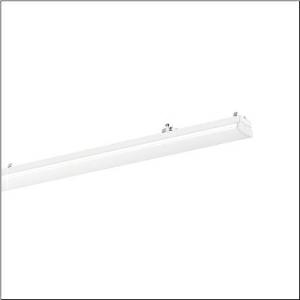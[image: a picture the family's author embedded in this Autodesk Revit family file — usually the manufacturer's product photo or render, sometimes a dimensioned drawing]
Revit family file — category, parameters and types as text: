
# Revit family: licross_21_recessed_opal_mo_52te1dcn485g
name_source: partatom
category: Lighting Fixtures
units: mm (PartAtom-declared; Revit-internal decimal feet)

## family parameters
Cut with Voids When Loaded = No
Host = Face
Light Source = No
Part Type = Normal
Room Calculation Point = No
Round Connector Dimension = Use Diameter
Shared = No

## types (1)
- --- (1 x LED, 8780 lm, 49.9 W, 4000K)
    Apparent Load = 50 VA
    CIE Flux Codes = 44 73 91 87 100
    Color Rendering = 80
    Color Temperature = 4000K
    Default Elevation = 1800 mm
    Description = Licross 21 recessed opal MO, luminaire insert, of sheet steel, galvanised, coil coated, white, length: 1.500mm, width: 66mm, height: 67mm, LED rated luminous flux: 8.780lm, light colour: 840, SDCM (Standard Deviation of Colour Matching)MacAdam ≤ 3 SDCM (initial), control gear: ON/OFF Multilumen, CLOi, with plug, 3-pole, with phase selection, mains connection: 220..240V, AC, 50/60Hz, start of lifetime: 50W, end of service life: 61W, internal wiring halogen-free, primary optical cover: cover, of PMMA, light emission: direct with ceiling illumination distribution, primary light characteristic: symmetric, protection rating (complete): IP54, insulation class (complete): insulation class I (protective earthing), certification: CE, ENEC, VDE, UKCA, protection symbol: D if used in an environment with non-conductive dust loads with corresponding accessories, impact resistance: IK06, permissible ambient temperature for indoor applications: -35..+40°C, corresponds to IFS (International Featured Standards) requirements for safety and quality in the food industry, reducing of maximum allowable ambient temperature of 5°C with ceiling mounting, LABS conformity tested according to VDMA 24364:2018-05, The light source and the operating device comply with the requirements of the Ecodesign Regulation (EU) 2019/2020 and are replaceable in accordance with this regulation, packaging unit: 1 piece
    Height = 83 mm
    Lamp = 1 x LED
    Lamp Light Flux = 8780 lm
    Lamp Power = 49.9 W
    Lamp count = 1
    Length = 1500 mm
    Luminous efficacy = 176 lm/W
    Manufacturer = Siteco
    ModVariant = No
    Model = 52TE1DCN485G
    Mounting Place = Ceiling
    Mounting Type = Pendant
    Number of Poles = 1
    OnlyDefault = Yes
    Power Factor = 1
    Product Name = Licross 21 recessed opal MO
    Product group = luminaire insert | ceiling pendant
    ProductGroupID = 901
    Protection Class = Protection class I
    Protection Degree = IP 54
    RLX_Detail_Level = 1
    RLX_Emergency_Light_Flux = 0 lm
    RLX_Emergency_Type = 0
    RLX_Emergency_Type_DB = No
    RlxData = <blob elided: 24953 chars, md5=fefaed7f>
    Socket = socket
    Standby Power = 0 W
    System Light Flux = 8780 lm
    System Power = 50 W
    Type Comments = factory setting: luminous flux: 100 % | (A | C | E) | 116 mA
    Type Image = l_1313666.jpg
    URL = http://relux.com
    VarID = @adj_075991
    Voltage = 0 V
    Weight = 0.00 kg
    Width = 76 mm

## geometry (parser evidence)
native form markers: Blend x4, Sweep x12
no freeform markers — native parametric forms only
